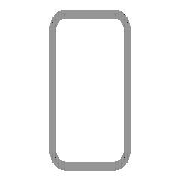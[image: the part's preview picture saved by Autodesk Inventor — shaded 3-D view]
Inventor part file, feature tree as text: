
AUTODESK INVENTOR PART (.ipt)
format: ipt  version: 2025 (Build 290162010, 162A)  size: 135,168 bytes
history: native  units: mm (DEFAULTED — no unit token found)
features: other x4, sketch x1, plane x1
ambient origin geometry x8: Origin, YZ Plane, XZ Plane, XY Plane, X Axis, Y Axis, Z Axis, Center Point
bodies: Solid1 (feature_tree), Body (feature_tree)
feature tree (6):
  parser-record x1  (decoder bookkeeping rows leaked as tree rows — omitted from the tree; the rows remain in map.json)
  other  "Driven Length"
  other  "Start Plane"
  other  "End Plane"
  sketch  "Sketch3"  dims[d3=1500.0mm d4=0.0mm d7=4.0mm d9=40.0mm d11=60.0mm d12=2.0mm d13=-0.0mm d14=1500.0mm d15=20.0mm d16=30.0mm d17=90.0deg d18=1500.0mm]
  plane  "Work Plane3"
